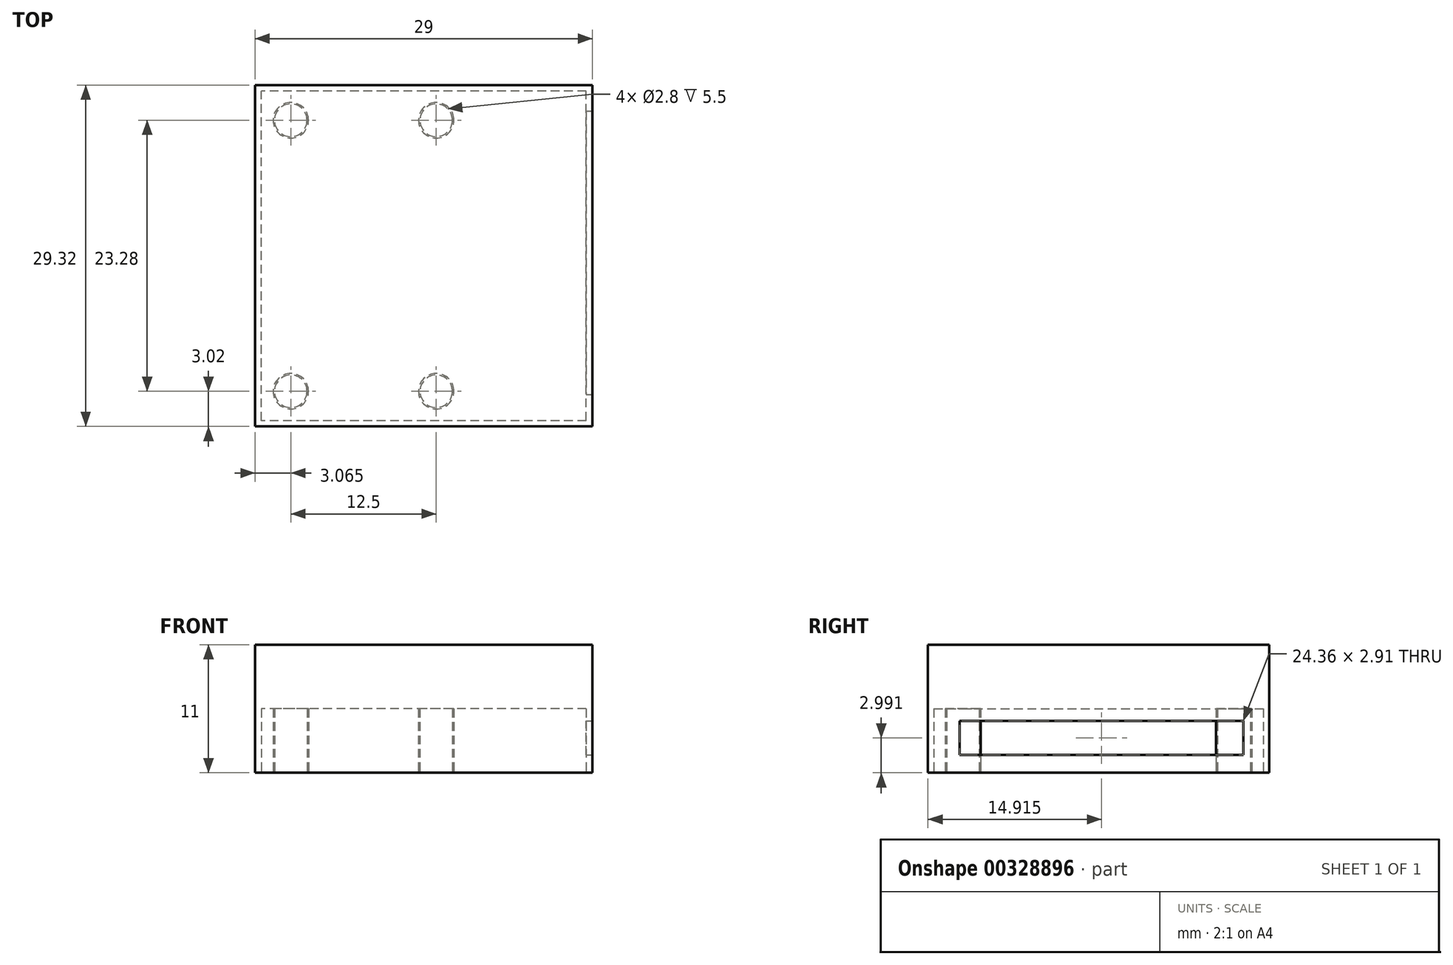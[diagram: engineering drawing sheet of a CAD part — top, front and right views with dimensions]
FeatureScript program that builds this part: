
annotation { "Feature Type Name" : "Feature", "Feature Type Description" : "" }
export const myFeature = defineFeature(function(context is Context, id is Id, definition is map)
    precondition{}
    {
        {
            var Q0;
            Q0=qCreatedBy(makeId("Top.planeOp"),FACE);
            var sketch = newSketch(context, id + "F0", { "sketchPlane" : qUnion([Q0])});
            skLineSegment(sketch, "E0.bottom", {"start": v(16.5, -13.16) * mm, "end": v(-12.5, -13.16) * mm});
            skLineSegment(sketch, "E0.top", {"start": v(16.5, 16.16) * mm, "end": v(-12.5, 16.16) * mm});
            skLineSegment(sketch, "E0.left", {"start": v(16.5, -13.16) * mm, "end": v(16.5, 16.16) * mm});
            skLineSegment(sketch, "E0.right", {"start": v(-12.5, -13.16) * mm, "end": v(-12.5, 16.16) * mm});
            skPoint(sketch, "E0.middle", {"position": v(0, 0) * mm});
            skLineSegment(sketch, "E1.bottom", {"start": v(15.96, -12.66) * mm, "end": v(-11.95, -12.66) * mm});
            skLineSegment(sketch, "E1.top", {"start": v(15.96, 15.66) * mm, "end": v(-11.95, 15.66) * mm});
            skLineSegment(sketch, "E1.left", {"start": v(15.96, -12.66) * mm, "end": v(15.96, 15.66) * mm});
            skLineSegment(sketch, "E1.right", {"start": v(-11.95, -12.66) * mm, "end": v(-11.96, 15.66) * mm});
            skPoint(sketch, "E1.middle", {"position": v(2, 1.5) * mm});
            skCircle(sketch, "E2", {"center": v(-9.43, 13.14) * mm, "radius": 1.4 * mm});
            skCircle(sketch, "E3", {"center": v(3.07, 13.14) * mm, "radius": 1.4 * mm});
            skCircle(sketch, "E4", {"center": v(-9.43, -10.14) * mm, "radius": 1.4 * mm});
            skCircle(sketch, "E5", {"center": v(3.07, -10.14) * mm, "radius": 1.4 * mm});
            skCircle(sketch, "E6", {"center": v(3.07, -10.14) * mm, "radius": 1.52 * mm});
            skCircle(sketch, "E7", {"center": v(-9.43, -10.14) * mm, "radius": 1.52 * mm});
            skCircle(sketch, "E8", {"center": v(3.07, 13.14) * mm, "radius": 1.52 * mm});
            skCircle(sketch, "E9", {"center": v(-9.43, 13.14) * mm, "radius": 1.52 * mm});
            skSolve(sketch);
        }
        {
            var Q0;
            Q0=makeQuery(id+"F0.imprint","IMPRINT",FACE,{"disambiguationData":[TD([[makeQuery(id+"F0.imprint","IMPRINT",EDGE,{"derivedFrom":sQuery(id+"F0.wireOp",EDGE,"E0.bottom")}),-1.0]])]});
            var Q1;
            Q1=makeQuery(id+"F0.imprint","IMPRINT",FACE,{"disambiguationData":[TD([[makeQuery(id+"F0.imprint","IMPRINT",EDGE,{"derivedFrom":sQuery(id+"F0.wireOp",EDGE,"E1.bottom")}),-1.0]])]});
            var Q2;
            Q2=makeQuery(id+"F0.imprint","IMPRINT",FACE,{"disambiguationData":[TD([[makeQuery(id+"F0.imprint","IMPRINT",EDGE,{"derivedFrom":sQuery(id+"F0.wireOp",EDGE,"E3")}),1.0]])]});
            var Q3;
            Q3=makeQuery(id+"F0.imprint","IMPRINT",FACE,{"disambiguationData":[TD([[makeQuery(id+"F0.imprint","IMPRINT",EDGE,{"derivedFrom":sQuery(id+"F0.wireOp",EDGE,"E3")}),-1.0]])]});
            var Q4;
            Q4=makeQuery(id+"F0.imprint","IMPRINT",FACE,{"disambiguationData":[TD([[makeQuery(id+"F0.imprint","IMPRINT",EDGE,{"derivedFrom":sQuery(id+"F0.wireOp",EDGE,"E5")}),1.0]])]});
            var Q5;
            Q5=makeQuery(id+"F0.imprint","IMPRINT",FACE,{"disambiguationData":[TD([[makeQuery(id+"F0.imprint","IMPRINT",EDGE,{"derivedFrom":sQuery(id+"F0.wireOp",EDGE,"E5")}),-1.0]])]});
            var Q6;
            Q6=makeQuery(id+"F0.imprint","IMPRINT",FACE,{"disambiguationData":[TD([[makeQuery(id+"F0.imprint","IMPRINT",EDGE,{"derivedFrom":sQuery(id+"F0.wireOp",EDGE,"E4")}),1.0]])]});
            var Q7;
            Q7=makeQuery(id+"F0.imprint","IMPRINT",FACE,{"disambiguationData":[TD([[makeQuery(id+"F0.imprint","IMPRINT",EDGE,{"derivedFrom":sQuery(id+"F0.wireOp",EDGE,"E4")}),-1.0]])]});
            var Q8;
            Q8=makeQuery(id+"F0.imprint","IMPRINT",FACE,{"disambiguationData":[TD([[makeQuery(id+"F0.imprint","IMPRINT",EDGE,{"derivedFrom":sQuery(id+"F0.wireOp",EDGE,"E2")}),1.0]])]});
            var Q9;
            Q9=makeQuery(id+"F0.imprint","IMPRINT",FACE,{"disambiguationData":[TD([[makeQuery(id+"F0.imprint","IMPRINT",EDGE,{"derivedFrom":sQuery(id+"F0.wireOp",EDGE,"E2")}),-1.0]])]});
            extrude(context, id + "F1", {"entities" : qUnion([Q0, Q1, Q2, Q3, Q4, Q5, Q6, Q7, Q8, Q9]), "depth" : 11 * mm});
        }
        {
            var Q0;
            Q0=makeQuery(id+"F0.imprint","IMPRINT",FACE,{"disambiguationData":[TD([[makeQuery(id+"F0.imprint","IMPRINT",EDGE,{"derivedFrom":sQuery(id+"F0.wireOp",EDGE,"E4")}),1.0]])]});
            var Q1;
            Q1=makeQuery(id+"F0.imprint","IMPRINT",FACE,{"disambiguationData":[TD([[makeQuery(id+"F0.imprint","IMPRINT",EDGE,{"derivedFrom":sQuery(id+"F0.wireOp",EDGE,"E5")}),1.0]])]});
            var Q2;
            Q2=makeQuery(id+"F0.imprint","IMPRINT",FACE,{"disambiguationData":[TD([[makeQuery(id+"F0.imprint","IMPRINT",EDGE,{"derivedFrom":sQuery(id+"F0.wireOp",EDGE,"E3")}),1.0]])]});
            var Q3;
            Q3=makeQuery(id+"F0.imprint","IMPRINT",FACE,{"disambiguationData":[TD([[makeQuery(id+"F0.imprint","IMPRINT",EDGE,{"derivedFrom":sQuery(id+"F0.wireOp",EDGE,"E2")}),1.0]])]});
            var Q4;
            Q4=makeQuery(id+"F0.imprint","IMPRINT",FACE,{"disambiguationData":[TD([[makeQuery(id+"F0.imprint","IMPRINT",EDGE,{"derivedFrom":sQuery(id+"F0.wireOp",EDGE,"E1.bottom")}),-1.0]])]});
            extrude(context, id + "F2", {"entities" : qUnion([Q0, Q1, Q2, Q3, Q4]), "operationType" : NewBodyOperationType.REMOVE, "depth" : 5.5 * mm});
        }
        {
            var Q0;
            Q0=makeQuery(id+"F1.opExtrude","SWEPT_FACE",FACE,{"disambiguationData":[OSD([sQuery(id+"F0.wireOp",EDGE,"E0.left")])]});
            var sketch = newSketch(context, id + "F3", { "sketchPlane" : qUnion([Q0])});
            skLineSegment(sketch, "E10.bottom", {"start": v(-10.43, 4.45) * mm, "end": v(13.93, 4.45) * mm});
            skLineSegment(sketch, "E10.top", {"start": v(-10.43, 1.53) * mm, "end": v(13.93, 1.53) * mm});
            skLineSegment(sketch, "E10.left", {"start": v(-10.43, 4.45) * mm, "end": v(-10.43, 1.53) * mm});
            skLineSegment(sketch, "E10.right", {"start": v(13.93, 4.45) * mm, "end": v(13.93, 1.53) * mm});
            skSolve(sketch);
        }
        {
            var Q0;
            Q0 = qSketchRegion(id + "F3", true);
            extrude(context, id + "F4", {"entities" : qUnion([Q0]), "operationType" : NewBodyOperationType.REMOVE, "oppositeDirection" : true, "depth" : 10 * mm});
        }
    });
